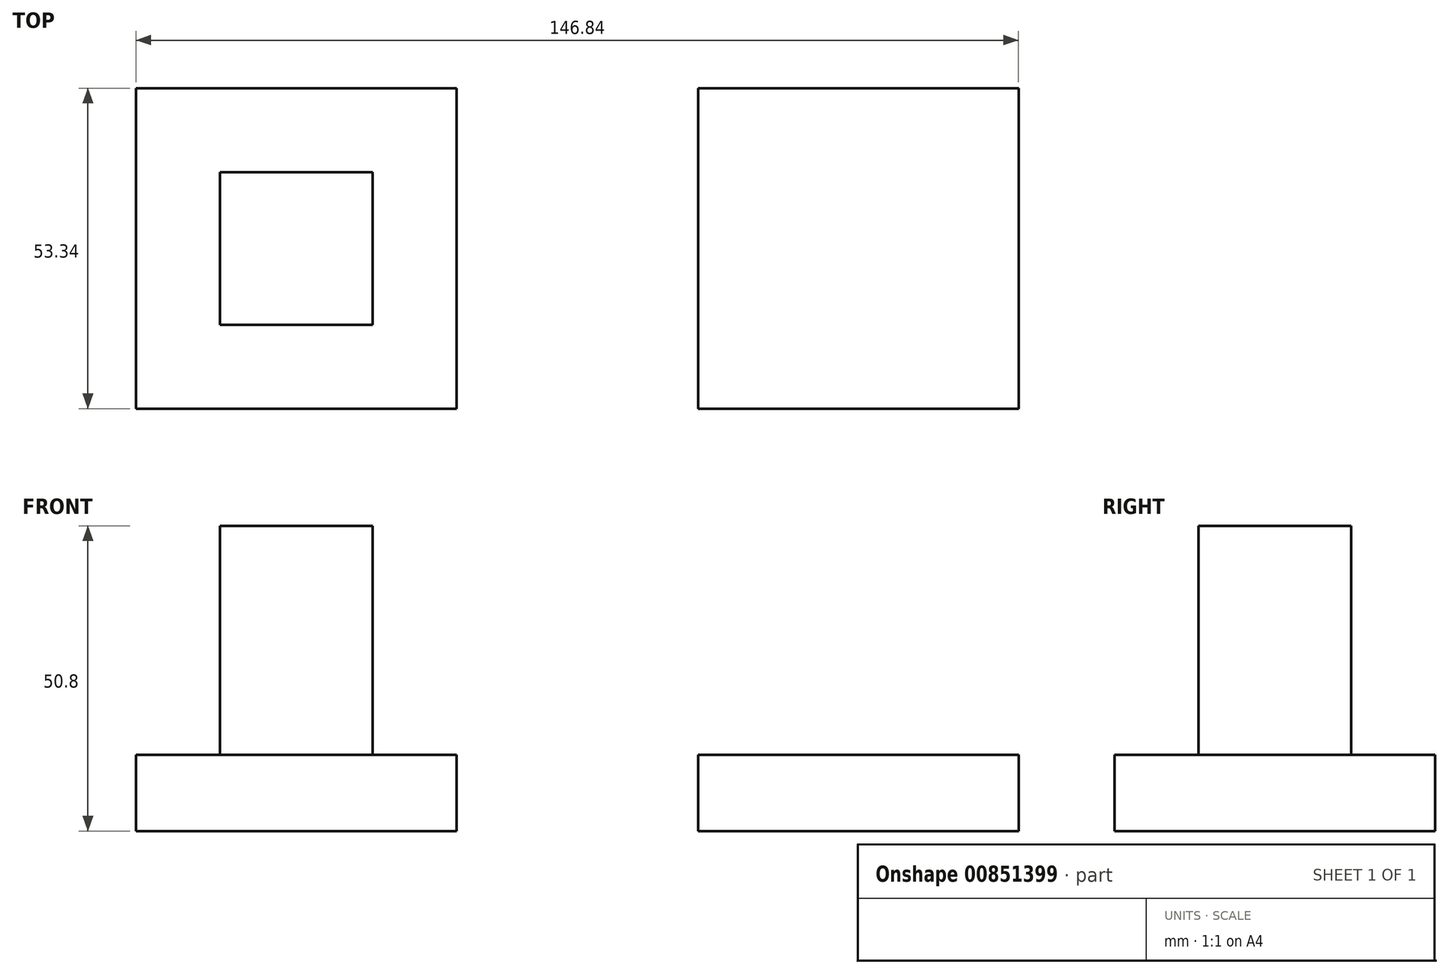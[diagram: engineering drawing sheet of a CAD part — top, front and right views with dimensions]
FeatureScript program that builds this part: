
annotation { "Feature Type Name" : "Feature", "Feature Type Description" : "" }
export const myFeature = defineFeature(function(context is Context, id is Id, definition is map)
    precondition{}
    {
        {
            var Q0;
            Q0=qCreatedBy(makeId("Top.planeOp"),FACE);
            var sketch = newSketch(context, id + "F0", { "sketchPlane" : qUnion([Q0])});
            skLineSegment(sketch, "E0.bottom", {"start": v(-73.42, 65.35) * mm, "end": v(-20.08, 65.35) * mm});
            skLineSegment(sketch, "E0.top", {"start": v(-73.42, 12) * mm, "end": v(-20.08, 12) * mm});
            skLineSegment(sketch, "E0.left", {"start": v(-73.42, 65.35) * mm, "end": v(-73.42, 12) * mm});
            skLineSegment(sketch, "E0.right", {"start": v(-20.08, 65.35) * mm, "end": v(-20.08, 12) * mm});
            skLineSegment(sketch, "E1.MirrorCS", {"start": v(20.08, 65.35) * mm, "end": v(20.08, 12) * mm});
            skLineSegment(sketch, "E2.MirrorCS", {"start": v(73.42, 65.35) * mm, "end": v(20.08, 65.35) * mm});
            skLineSegment(sketch, "E3.MirrorCS", {"start": v(73.42, 65.35) * mm, "end": v(73.42, 12) * mm});
            skLineSegment(sketch, "E4.MirrorCS", {"start": v(73.42, 12) * mm, "end": v(20.08, 12) * mm});
            skLineSegment(sketch, "E5.bottom", {"start": v(-59.45, 51.38) * mm, "end": v(-34.05, 51.38) * mm});
            skLineSegment(sketch, "E5.top", {"start": v(-59.45, 25.98) * mm, "end": v(-34.05, 25.98) * mm});
            skLineSegment(sketch, "E5.left", {"start": v(-59.45, 51.38) * mm, "end": v(-59.45, 25.98) * mm});
            skLineSegment(sketch, "E5.right", {"start": v(-34.05, 51.38) * mm, "end": v(-34.05, 25.98) * mm});
            skSolve(sketch);
        }
        {
            var Q0;
            Q0 = qSketchRegion(id + "F0", true);
            extrude(context, id + "F1", {"entities" : qUnion([Q0]), "depth" : 12.7 * mm, "offsetDistance" : 25.4 * mm});
        }
        {
            var Q0;
            Q0=makeQuery(id+"F0.imprint","IMPRINT",FACE,{"disambiguationData":[TD([[makeQuery(id+"F0.imprint","IMPRINT",EDGE,{"derivedFrom":sQuery(id+"F0.wireOp",EDGE,"E5.bottom")}),-1.0]])]});
            extrude(context, id + "F2", {"entities" : qUnion([Q0]), "operationType" : NewBodyOperationType.ADD, "depth" : 50.8 * mm, "offsetDistance" : 25.4 * mm});
        }
    });
